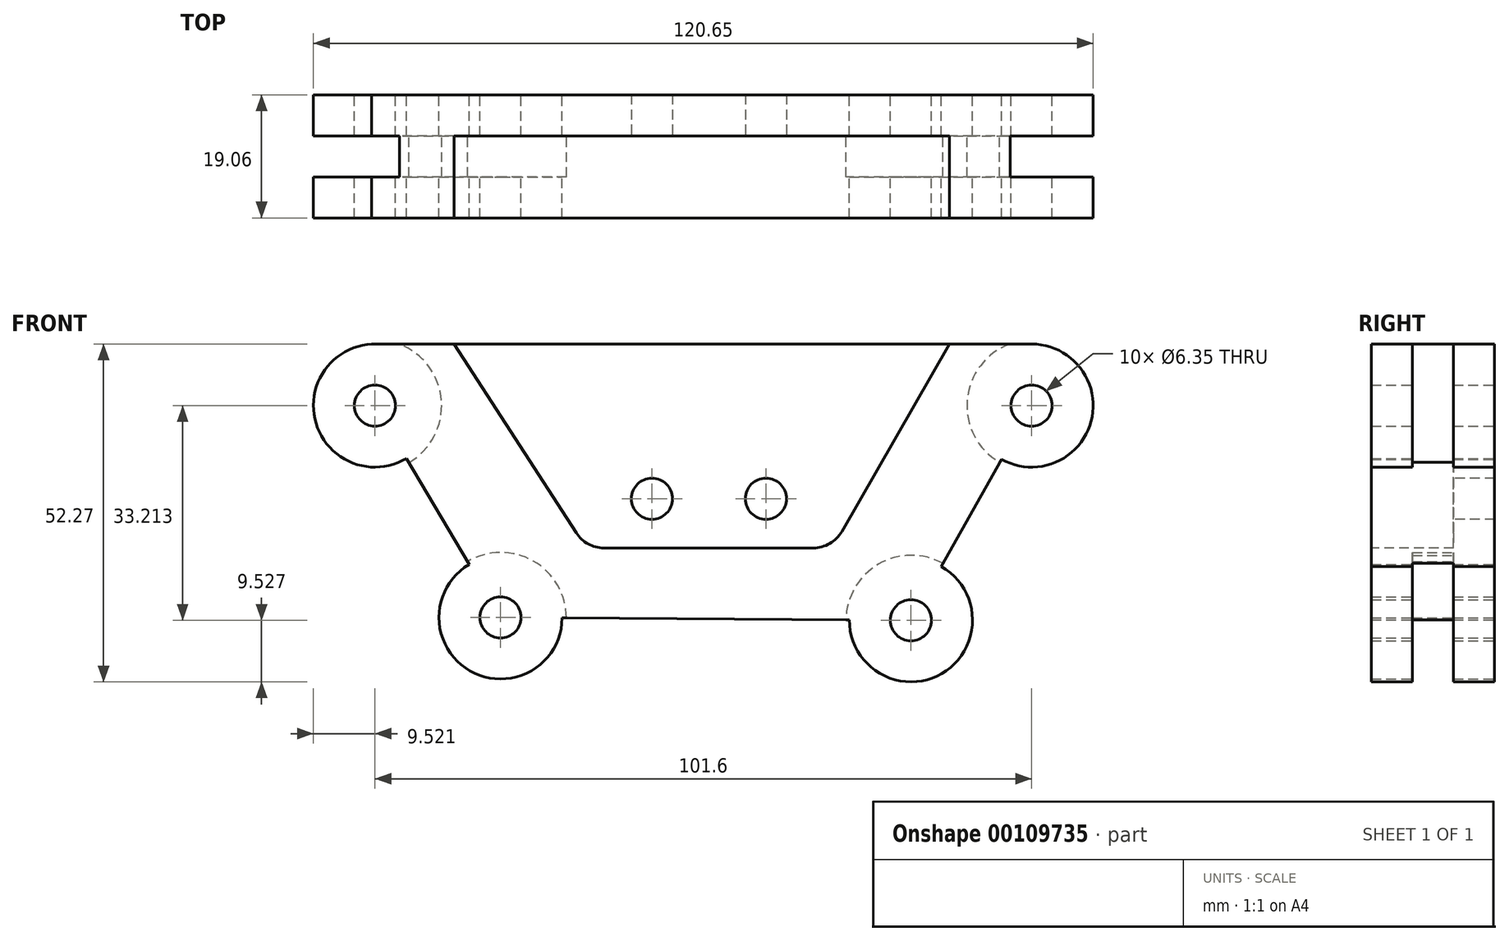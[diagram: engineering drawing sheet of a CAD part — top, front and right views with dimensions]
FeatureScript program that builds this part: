
annotation { "Feature Type Name" : "Feature", "Feature Type Description" : "" }
export const myFeature = defineFeature(function(context is Context, id is Id, definition is map)
    precondition{}
    {
        {
            var Q0;
            Q0=qCreatedBy(makeId("Front.planeOp"),FACE);
            var sketch = newSketch(context, id + "F0", { "sketchPlane" : qUnion([Q0])});
            skCircle(sketch, "E0", {"center": v(-51.36, 0) * mm, "radius": 9.53 * mm});
            skCircle(sketch, "E1", {"center": v(-51.36, 0) * mm, "radius": 3.18 * mm});
            skCircle(sketch, "E2", {"center": v(50.24, 0) * mm, "radius": 9.53 * mm});
            skCircle(sketch, "E3", {"center": v(50.24, 0) * mm, "radius": 3.18 * mm});
            skLineSegment(sketch, "E4", {"start": v(0, 0) * mm, "end": v(-0.56, -33.21) * mm, "construction": true});
            skPoint(sketch, "E4.endSnap0", {"position": v(-0.56, 0) * mm});
            skCircle(sketch, "E5", {"center": v(-31.93, -32.77) * mm, "radius": 9.53 * mm});
            skCircle(sketch, "E6", {"center": v(-31.93, -32.77) * mm, "radius": 3.18 * mm});
            skCircle(sketch, "E7", {"center": v(31.57, -33.21) * mm, "radius": 9.53 * mm});
            skCircle(sketch, "E8", {"center": v(31.57, -33.21) * mm, "radius": 3.18 * mm});
            skLineSegment(sketch, "E9", {"start": v(-51.36, 0) * mm, "end": v(-31.93, -32.77) * mm});
            skLineSegment(sketch, "E10", {"start": v(31.57, -33.21) * mm, "end": v(50.24, 0) * mm});
            skLineSegment(sketch, "E11", {"start": v(31.57, -33.21) * mm, "end": v(-31.93, -32.77) * mm});
            skLineSegment(sketch, "E12", {"start": v(-51.85, 9.51) * mm, "end": v(50.24, 9.52) * mm});
            skSolve(sketch);
        }
        {
            var Q0;
            {var subQ0=sQuery(id+"F0.wireOp",EDGE,"XNQRTcA6-6CWJ-eaxb-RzQE-zFXrrv5FkplZ");var subQ1=sQuery(id+"F0.wireOp",EDGE,"E0");var subQ2=makeQuery(id+"F0.imprint","INTERSECT",VERTEX,{"derivedFrom":[subQ1,subQ0]});Q0=makeQuery(id+"F0.imprint","IMPRINT",FACE,{"disambiguationData":[TD([[makeQuery(id+"F0.imprint","IMPRINT",EDGE,{"disambiguationData":[TD([[subQ2,-1.0]])],"derivedFrom":subQ1}),1.0]])]});}
            var Q1;
            {var subQ0=sQuery(id+"F0.wireOp",EDGE,"XNQRTcA6-6CWJ-eaxb-RzQE-zFXrrv5FkplZ");var subQ1=sQuery(id+"F0.wireOp",EDGE,"E0");var subQ2=makeQuery(id+"F0.imprint","INTERSECT",VERTEX,{"derivedFrom":[subQ1,subQ0]});Q1=makeQuery(id+"F0.imprint","IMPRINT",FACE,{"disambiguationData":[TD([[makeQuery(id+"F0.imprint","IMPRINT",EDGE,{"disambiguationData":[TD([[subQ2,1.0]])],"derivedFrom":subQ1}),1.0]])]});}
            var Q2;
            {var subQ5=sQuery(id+"F0.wireOp",EDGE,"XNQRTcA6-6CWJ-eaxb-RzQE-zFXrrv5FkplZ");var subQ6=sQuery(id+"F0.wireOp",EDGE,"E0");var subQ7=makeQuery(id+"F0.imprint","INTERSECT",VERTEX,{"derivedFrom":[subQ6,subQ5]});Q2=makeQuery(id+"F0.imprint","IMPRINT",FACE,{"disambiguationData":[TD([[makeQuery(id+"F0.imprint","IMPRINT",EDGE,{"disambiguationData":[TD([[subQ7,1.0]])],"derivedFrom":subQ6}),-1.0]])]});}
            var Q3;
            {var subQ0=sQuery(id+"F0.wireOp",EDGE,"E9");var subQ1=sQuery(id+"F0.wireOp",EDGE,"E5");var subQ2=makeQuery(id+"F0.imprint","INTERSECT",VERTEX,{"derivedFrom":[subQ1,subQ0]});Q3=makeQuery(id+"F0.imprint","IMPRINT",FACE,{"disambiguationData":[TD([[makeQuery(id+"F0.imprint","IMPRINT",EDGE,{"disambiguationData":[TD([[subQ2,-1.0]])],"derivedFrom":subQ1}),1.0]])]});}
            var Q4;
            {var subQ0=sQuery(id+"F0.wireOp",EDGE,"E9");var subQ1=sQuery(id+"F0.wireOp",EDGE,"E5");var subQ2=makeQuery(id+"F0.imprint","INTERSECT",VERTEX,{"derivedFrom":[subQ1,subQ0]});Q4=makeQuery(id+"F0.imprint","IMPRINT",FACE,{"disambiguationData":[TD([[makeQuery(id+"F0.imprint","IMPRINT",EDGE,{"disambiguationData":[TD([[subQ2,1.0]])],"derivedFrom":subQ1}),1.0]])]});}
            var Q5;
            {var subQ0=sQuery(id+"F0.wireOp",EDGE,"E10");var subQ1=sQuery(id+"F0.wireOp",EDGE,"E7");var subQ2=makeQuery(id+"F0.imprint","INTERSECT",VERTEX,{"derivedFrom":[subQ1,subQ0]});Q5=makeQuery(id+"F0.imprint","IMPRINT",FACE,{"disambiguationData":[TD([[makeQuery(id+"F0.imprint","IMPRINT",EDGE,{"disambiguationData":[TD([[subQ2,-1.0]])],"derivedFrom":subQ1}),1.0]])]});}
            var Q6;
            {var subQ0=sQuery(id+"F0.wireOp",EDGE,"E10");var subQ1=sQuery(id+"F0.wireOp",EDGE,"E7");var subQ2=makeQuery(id+"F0.imprint","INTERSECT",VERTEX,{"derivedFrom":[subQ1,subQ0]});Q6=makeQuery(id+"F0.imprint","IMPRINT",FACE,{"disambiguationData":[TD([[makeQuery(id+"F0.imprint","IMPRINT",EDGE,{"disambiguationData":[TD([[subQ2,1.0]])],"derivedFrom":subQ1}),1.0]])]});}
            var Q7;
            {var subQ0=sQuery(id+"F0.wireOp",EDGE,"XNQRTcA6-6CWJ-eaxb-RzQE-zFXrrv5FkplZ");var subQ1=sQuery(id+"F0.wireOp",EDGE,"E2");var subQ2=makeQuery(id+"F0.imprint","INTERSECT",VERTEX,{"derivedFrom":[subQ1,subQ0]});Q7=makeQuery(id+"F0.imprint","IMPRINT",FACE,{"disambiguationData":[TD([[makeQuery(id+"F0.imprint","IMPRINT",EDGE,{"disambiguationData":[TD([[subQ2,-1.0]])],"derivedFrom":subQ1}),1.0]])]});}
            var Q8;
            {var subQ0=sQuery(id+"F0.wireOp",EDGE,"XNQRTcA6-6CWJ-eaxb-RzQE-zFXrrv5FkplZ");var subQ1=sQuery(id+"F0.wireOp",EDGE,"E2");var subQ2=makeQuery(id+"F0.imprint","INTERSECT",VERTEX,{"derivedFrom":[subQ1,subQ0]});Q8=makeQuery(id+"F0.imprint","IMPRINT",FACE,{"disambiguationData":[TD([[makeQuery(id+"F0.imprint","IMPRINT",EDGE,{"disambiguationData":[TD([[subQ2,1.0]])],"derivedFrom":subQ1}),1.0]])]});}
            extrude(context, id + "F1", {"entities" : qUnion([Q0, Q1, Q2, Q3, Q4, Q5, Q6, Q7, Q8]), "endBound" : BoundingType.SYMMETRIC, "depth" : 19.05 * mm});
        }
        {
            var Q0;
            Q0=makeQuery(id+"F1.opExtrude","CAP_FACE",FACE,{"disambiguationData":[OSD([sQuery(id+"F0.wireOp",EDGE,"E0"),sQuery(id+"F0.wireOp",EDGE,"E1"),sQuery(id+"F0.wireOp",EDGE,"E2"),sQuery(id+"F0.wireOp",EDGE,"E3"),sQuery(id+"F0.wireOp",EDGE,"E5"),sQuery(id+"F0.wireOp",EDGE,"E6"),sQuery(id+"F0.wireOp",EDGE,"E7"),sQuery(id+"F0.wireOp",EDGE,"E8"),sQuery(id+"F0.wireOp",EDGE,"E9"),sQuery(id+"F0.wireOp",EDGE,"E10"),sQuery(id+"F0.wireOp",EDGE,"E11"),sQuery(id+"F0.wireOp",EDGE,"E12")])],"isStart":false});
            var sketch = newSketch(context, id + "F2", { "sketchPlane" : qUnion([Q0])});
            skLineSegment(sketch, "E13", {"start": v(-39.15, 9.51) * mm, "end": v(-18.7, -22.03) * mm});
            skLineSegment(sketch, "E14", {"start": v(-18.7, -22.03) * mm, "end": v(19.4, -22.03) * mm});
            skLineSegment(sketch, "E15", {"start": v(19.4, -22.03) * mm, "end": v(37.54, 9.52) * mm});
            skSolve(sketch);
        }
        {
            var Q0;
            Q0 = qSketchRegion(id + "F2", true);
            var Q1;
            {var subQ0=sQuery(id+"F2.wireOp",EDGE,"E13");Q1=makeQuery(id+"F2.imprint","IMPRINT",FACE,{"disambiguationData":[TD([[makeQuery(id+"F2.imprint","IMPRINT",EDGE,{"derivedFrom":subQ0}),1.0]])]});}
            extrude(context, id + "F3", {"entities" : qUnion([Q0, Q1]), "operationType" : NewBodyOperationType.REMOVE, "oppositeDirection" : true, "depth" : 12.7 * mm});
        }
        {
            var Q0;
            Q0=qCreatedBy(makeId("Front.planeOp"),FACE);
            var sketch = newSketch(context, id + "F4", { "sketchPlane" : qUnion([Q0])});
            skCircle(sketch, "E16", {"center": v(-51.23, 0) * mm, "radius": 10.2 * mm});
            skCircle(sketch, "E17", {"center": v(50.37, 0) * mm, "radius": 10.13 * mm});
            skCircle(sketch, "E18", {"center": v(31.65, -33.31) * mm, "radius": 10.14 * mm});
            skCircle(sketch, "E19", {"center": v(-31.9, -32.9) * mm, "radius": 10.17 * mm});
            skSolve(sketch);
        }
        {
            var Q0;
            Q0 = qSketchRegion(id + "F4", true);
            extrude(context, id + "F5", {"entities" : qUnion([Q0]), "operationType" : NewBodyOperationType.REMOVE, "endBound" : BoundingType.SYMMETRIC, "depth" : 6.35 * mm});
        }
        {
            var Q0;
            Q0=makeQuery(id+"F3.boolean.opBoolean","COPY",FACE,{"derivedFrom":makeQuery(id+"F3.opExtrude","CAP_FACE",FACE,{"disambiguationData":[OSD([sQuery(id+"F0.wireOp",EDGE,"E12"),sQuery(id+"F2.wireOp",EDGE,"E13"),sQuery(id+"F2.wireOp",EDGE,"E14"),sQuery(id+"F2.wireOp",EDGE,"E15")])],"isStart":false})});
            var sketch = newSketch(context, id + "F6", { "sketchPlane" : qUnion([Q0])});
            skCircle(sketch, "E20", {"center": v(-8.5, -14.4) * mm, "radius": 3.18 * mm});
            skCircle(sketch, "E21", {"center": v(9.14, -14.4) * mm, "radius": 3.18 * mm});
            skSolve(sketch);
        }
        {
            var Q0;
            Q0 = qSketchRegion(id + "F6", true);
            extrude(context, id + "F7", {"entities" : qUnion([Q0]), "operationType" : NewBodyOperationType.REMOVE, "oppositeDirection" : true, "depth" : 8.76 * mm});
        }
        {
            var Q0;
            Q0=makeQuery(id+"F3.boolean.opBoolean","COPY",EDGE,{"derivedFrom":makeQuery(id+"F3.opExtrude","SWEPT_EDGE",EDGE,{"disambiguationData":[OSD([sQuery(id+"F2.wireOp",EDGE,"E13"),sQuery(id+"F2.wireOp",EDGE,"E14")])]})});
            var Q1;
            Q1=makeQuery(id+"F3.boolean.opBoolean","COPY",EDGE,{"derivedFrom":makeQuery(id+"F3.opExtrude","SWEPT_EDGE",EDGE,{"disambiguationData":[OSD([sQuery(id+"F2.wireOp",EDGE,"E14"),sQuery(id+"F2.wireOp",EDGE,"E15")])]})});
            var Q2;
            Q2=makeQuery(id+"F3.boolean.opBoolean","COPY",EDGE,{"derivedFrom":makeQuery(id+"F3.opExtrude","SWEPT_EDGE",EDGE,{"disambiguationData":[OSD([sQuery(id+"F0.wireOp",EDGE,"E12"),sQuery(id+"F2.wireOp",EDGE,"E15")])]})});
            var Q3;
            Q3=makeQuery(id+"F3.boolean.opBoolean","COPY",EDGE,{"derivedFrom":makeQuery(id+"F3.opExtrude","SWEPT_EDGE",EDGE,{"disambiguationData":[OSD([sQuery(id+"F0.wireOp",EDGE,"E12"),sQuery(id+"F2.wireOp",EDGE,"E13")])]})});
            fillet(context, id + "F8", {"entities" : qUnion([Q0, Q1, Q2, Q3]), "radius" : 5.08 * mm, "tangentPropagation" : true, "allowEdgeOverflow" : false});
        }
    });
